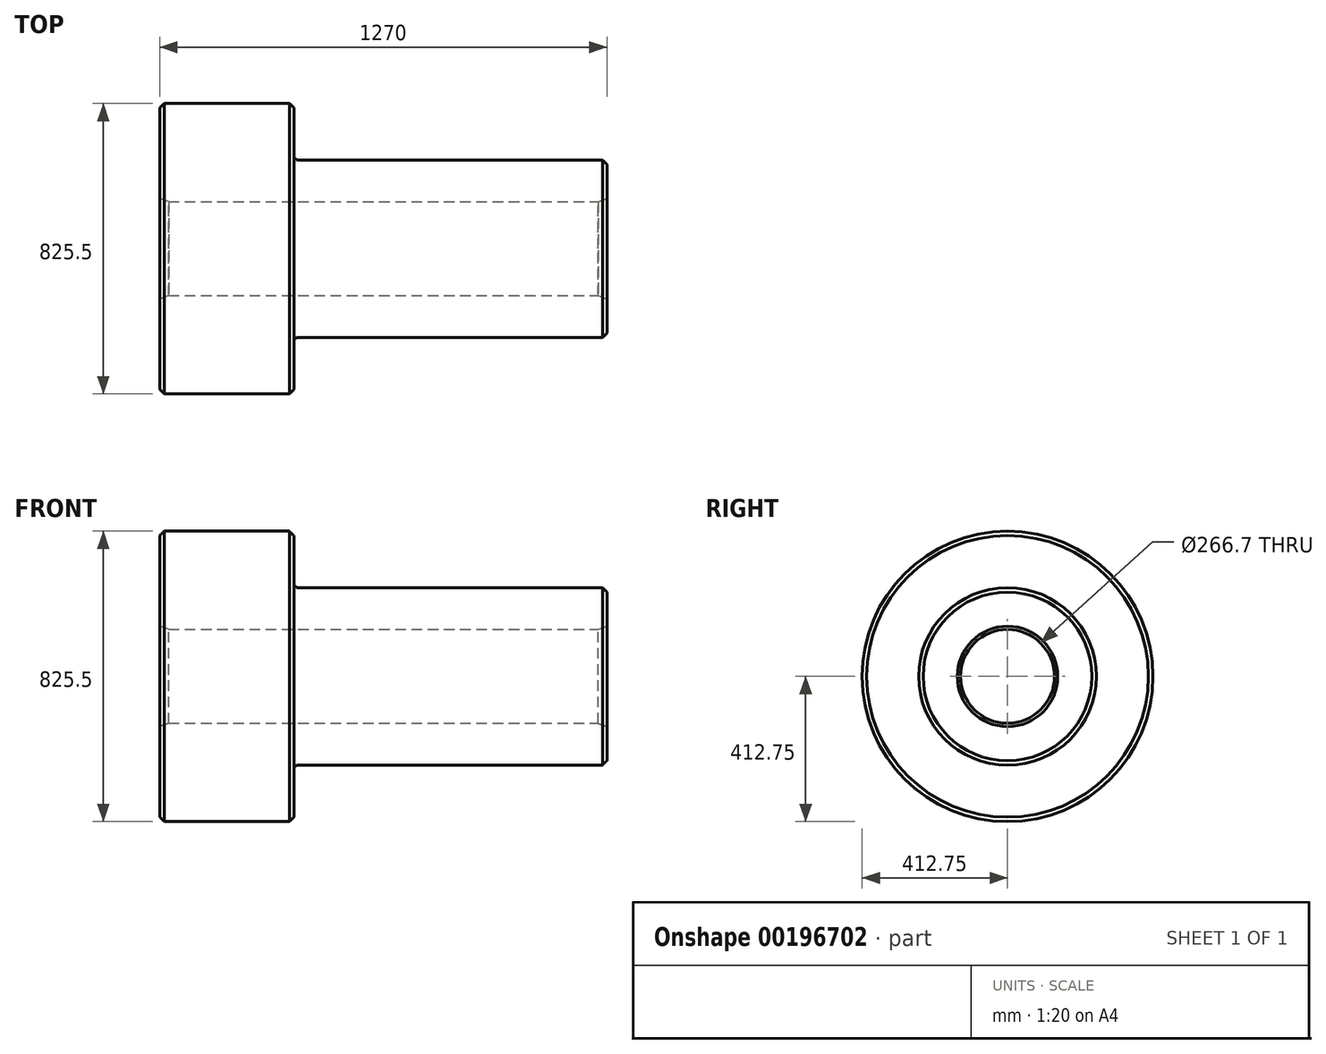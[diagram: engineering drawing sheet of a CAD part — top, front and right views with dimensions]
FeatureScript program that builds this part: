
annotation { "Feature Type Name" : "Feature", "Feature Type Description" : "" }
export const myFeature = defineFeature(function(context is Context, id is Id, definition is map)
    precondition{}
    {
        {
            var Q0;
            Q0=qCreatedBy(makeId("Front.planeOp"),FACE);
            var sketch = newSketch(context, id + "F0", { "sketchPlane" : qUnion([Q0])});
            skLineSegment(sketch, "E0", {"start": v(0, 142.6) * mm, "end": v(0, 252.29) * mm});
            skLineSegment(sketch, "E1", {"start": v(0, 252.29) * mm, "end": v(-876.3, 252.29) * mm});
            skLineSegment(sketch, "E2", {"start": v(-889, 412.75) * mm, "end": v(-889, 264.99) * mm});
            skLineSegment(sketch, "E3", {"start": v(-889, 412.75) * mm, "end": v(-1270, 412.75) * mm});
            skLineSegment(sketch, "E4", {"start": v(-1270, 412.75) * mm, "end": v(-1270, 142.6) * mm});
            skLineSegment(sketch, "E5", {"start": v(-1244.6, 133.35) * mm, "end": v(-25.4, 133.35) * mm});
            skLineSegment(sketch, "E6", {"start": v(-25.4, 133.35) * mm, "end": v(0, 142.6) * mm});
            skLineSegment(sketch, "E7", {"start": v(-1270, 142.6) * mm, "end": v(-1244.6, 133.35) * mm});
            skPoint(sketch, "E8.orphan", {"position": v(0, 133.35) * mm});
            skPoint(sketch, "E9.orphan", {"position": v(-1270, 133.35) * mm});
            skPoint(sketch, "E10.visualSharp", {"position": v(-889, 252.29) * mm});
            skArc(sketch, "E10.filletArc", {"start": v(-889, 264.99) * mm, "mid": v(-885.28, 256) * mm, "end": v(-876.3, 252.29) * mm});
            skLineSegment(sketch, "E11", {"start": v(0, 0) * mm, "end": v(-381, 0) * mm, "construction": true});
            skSolve(sketch);
        }
        {
            var Q0;
            Q0=makeQuery(id+"F0.imprint","IMPRINT",FACE,{"disambiguationData":[TD([[makeQuery(id+"F0.imprint","IMPRINT",EDGE,{"derivedFrom":sQuery(id+"F0.wireOp",EDGE,"E0")}),1.0]])]});
            var Q1;
            Q1=sQuery(id+"F0.wireOp",EDGE,"E11");
            revolve(context, id + "F1", {"entities" : qUnion([Q0]), "axis" : qUnion([Q1]), "revolveType" : RevolveType.FULL});
        }
        {
            var Q0;
            Q0=makeQuery(id+"F1.opRevolve","SWEPT_EDGE",EDGE,{"disambiguationData":[OSD([sQuery(id+"F0.wireOp",EDGE,"E0"),sQuery(id+"F0.wireOp",EDGE,"E1")])]});
            var Q1;
            Q1=makeQuery(id+"F1.opRevolve","SWEPT_EDGE",EDGE,{"disambiguationData":[OSD([sQuery(id+"F0.wireOp",EDGE,"E2"),sQuery(id+"F0.wireOp",EDGE,"E3")])]});
            var Q2;
            Q2=makeQuery(id+"F1.opRevolve","SWEPT_EDGE",EDGE,{"disambiguationData":[OSD([sQuery(id+"F0.wireOp",EDGE,"E3"),sQuery(id+"F0.wireOp",EDGE,"E4")])]});
            chamfer(context, id + "F2", {"entities" : qUnion([Q0, Q1, Q2]), "width" : 12.7 * mm, "tangentPropagation" : true});
        }
    });
